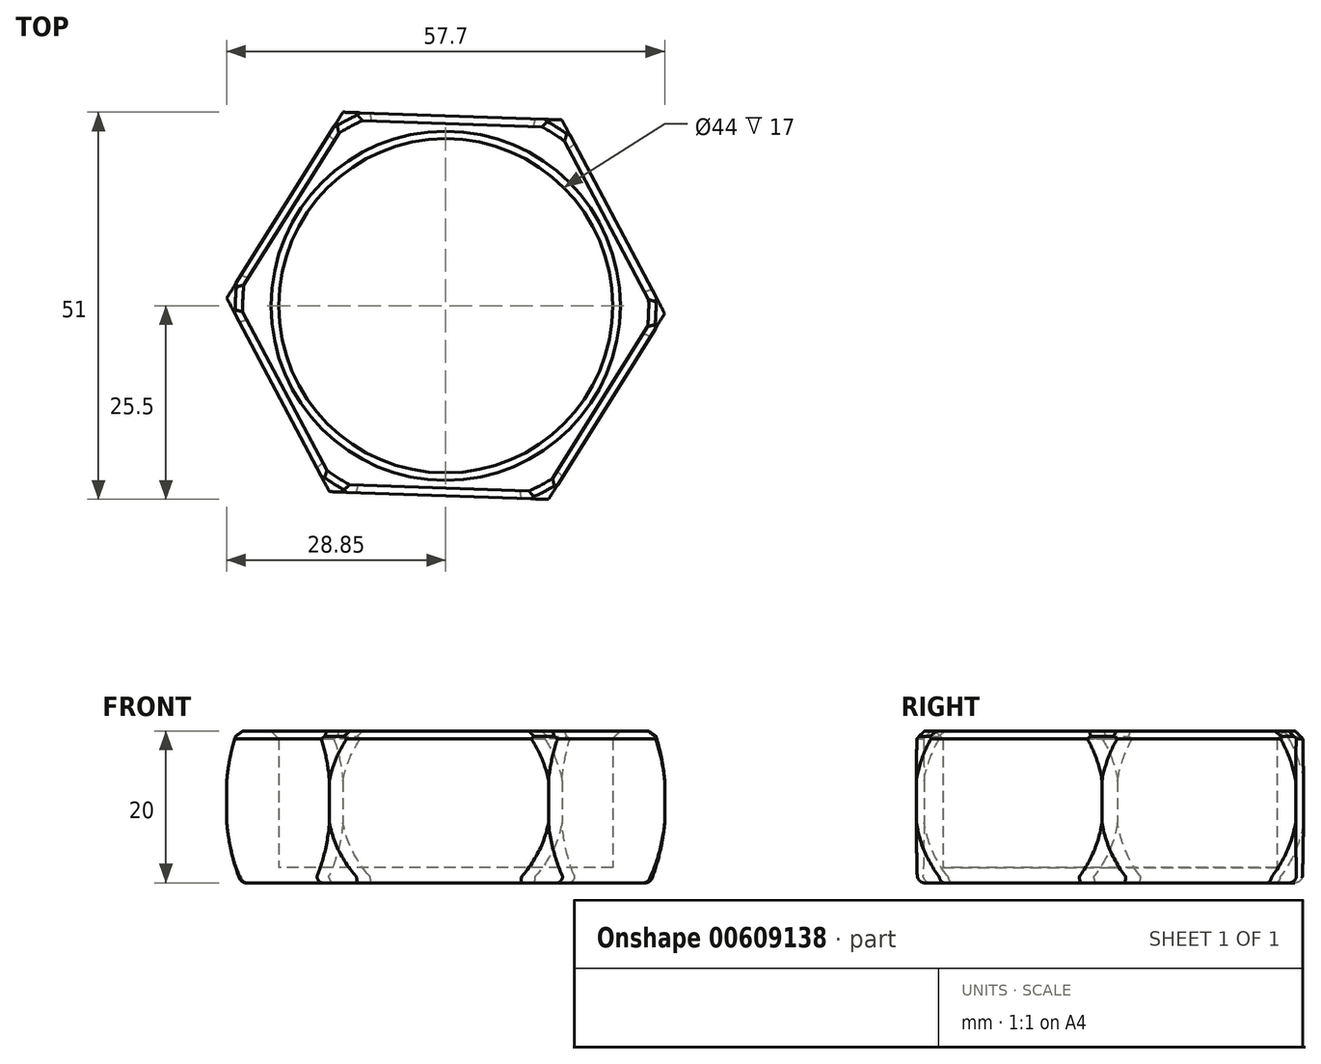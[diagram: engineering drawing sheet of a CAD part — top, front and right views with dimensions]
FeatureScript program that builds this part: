
annotation { "Feature Type Name" : "Feature", "Feature Type Description" : "" }
export const myFeature = defineFeature(function(context is Context, id is Id, definition is map)
    precondition{}
    {
        {
            var Q0;
            Q0=qCreatedBy(makeId("Top.planeOp"),FACE);
            var sketch = newSketch(context, id + "F0", { "sketchPlane" : qUnion([Q0])});
            skCircle(sketch, "E0.cCircle", {"center": v(0, 0) * mm, "radius": 25 * mm, "construction": true});
            skLineSegment(sketch, "E0.0", {"start": v(28.85, -1.03) * mm, "end": v(13.54, -25.5) * mm});
            skLineSegment(sketch, "E0.1", {"start": v(13.54, -25.5) * mm, "end": v(-15.31, -24.47) * mm});
            skLineSegment(sketch, "E0.2", {"start": v(-15.31, -24.47) * mm, "end": v(-28.85, 1.03) * mm});
            skLineSegment(sketch, "E0.3", {"start": v(-28.85, 1.03) * mm, "end": v(-13.54, 25.5) * mm});
            skLineSegment(sketch, "E0.4", {"start": v(-13.54, 25.5) * mm, "end": v(15.31, 24.47) * mm});
            skLineSegment(sketch, "E0.5", {"start": v(15.31, 24.47) * mm, "end": v(28.85, -1.03) * mm});
            skPoint(sketch, "E0.0.midPoint", {"position": v(21.2, -13.26) * mm});
            skSolve(sketch);
        }
        {
            var Q0;
            Q0 = qSketchRegion(id + "F0", true);
            var Q1;
            Q1=makeQuery(id+"F0.imprint","IMPRINT",FACE,{"disambiguationData":[TD([[makeQuery(id+"F0.imprint","IMPRINT",EDGE,{"derivedFrom":sQuery(id+"F0.wireOp",EDGE,"E0.0")}),-1.0]])]});
            extrude(context, id + "F1", {"entities" : qUnion([Q0, Q1]), "depth" : 2 * mm, "offsetDistance" : 25 * mm});
        }
        {
            var Q0;
            Q0=makeQuery(id+"F1.opExtrude","CAP_FACE",FACE,{"disambiguationData":[OSD([sQuery(id+"F0.wireOp",EDGE,"E0.0"),sQuery(id+"F0.wireOp",EDGE,"E0.1"),sQuery(id+"F0.wireOp",EDGE,"E0.2"),sQuery(id+"F0.wireOp",EDGE,"E0.3"),sQuery(id+"F0.wireOp",EDGE,"E0.4"),sQuery(id+"F0.wireOp",EDGE,"E0.5")])],"isStart":false});
            var sketch = newSketch(context, id + "F2", { "sketchPlane" : qUnion([Q0])});
            skLineSegment(sketch, "E1.0", {"start": v(13.54, -25.5) * mm, "end": v(28.85, -1.03) * mm});
            skLineSegment(sketch, "E1.1", {"start": v(15.31, 24.47) * mm, "end": v(-13.54, 25.5) * mm});
            skLineSegment(sketch, "E1.2", {"start": v(-13.54, 25.5) * mm, "end": v(-28.85, 1.03) * mm});
            skLineSegment(sketch, "E1.3", {"start": v(28.85, -1.03) * mm, "end": v(15.31, 24.47) * mm});
            skLineSegment(sketch, "E1.4", {"start": v(-28.85, 1.03) * mm, "end": v(-15.31, -24.47) * mm});
            skLineSegment(sketch, "E1.5", {"start": v(-15.31, -24.47) * mm, "end": v(13.54, -25.5) * mm});
            skCircle(sketch, "E2", {"center": v(0, 0) * mm, "radius": 22 * mm});
            skSolve(sketch);
        }
        {
            var Q0;
            Q0=makeQuery(id+"F2.imprint","IMPRINT",FACE,{"disambiguationData":[TD([[makeQuery(id+"F2.imprint","IMPRINT",EDGE,{"derivedFrom":sQuery(id+"F2.wireOp",EDGE,"E1.0")}),-1.0]])]});
            extrude(context, id + "F3", {"entities" : qUnion([Q0]), "operationType" : NewBodyOperationType.ADD, "depth" : 18 * mm, "offsetDistance" : 25 * mm});
        }
        {
            var Q0;
            Q0=qCreatedBy(makeId("Front.planeOp"),FACE);
            var sketch = newSketch(context, id + "F4", { "sketchPlane" : qUnion([Q0])});
            skArc(sketch, "E3", {"start": v(-4.27, 39.4) * mm, "mid": v(-27.23, 20.67) * mm, "end": v(-21.77, -8.45) * mm});
            skLineSegment(sketch, "E4", {"start": v(-4.27, 39.4) * mm, "end": v(-38.78, 38.35) * mm});
            skLineSegment(sketch, "E5", {"start": v(-38.78, 38.35) * mm, "end": v(-37.35, -8.92) * mm});
            skLineSegment(sketch, "E6", {"start": v(-37.35, -8.92) * mm, "end": v(-21.77, -8.45) * mm});
            skLineSegment(sketch, "E7", {"start": v(0, 10.7) * mm, "end": v(0, -7.35) * mm});
            skSolve(sketch);
        }
        {
            var Q0;
            Q0 = qSketchRegion(id + "F4", true);
            var Q1;
            Q1=sQuery(id+"F4.wireOp",EDGE,"E7");
            revolve(context, id + "F5", {"operationType" : NewBodyOperationType.REMOVE, "entities" : qUnion([Q0]), "axis" : qUnion([Q1]), "revolveType" : RevolveType.FULL, "oppositeDirection" : true});
        }
        {
            var Q0;
            Q0=makeQuery(id+"F1.opExtrude","CAP_FACE",FACE,{"disambiguationData":[OSD([sQuery(id+"F0.wireOp",EDGE,"E0.0"),sQuery(id+"F0.wireOp",EDGE,"E0.1"),sQuery(id+"F0.wireOp",EDGE,"E0.2"),sQuery(id+"F0.wireOp",EDGE,"E0.3"),sQuery(id+"F0.wireOp",EDGE,"E0.4"),sQuery(id+"F0.wireOp",EDGE,"E0.5")])],"isStart":true});
            fillet(context, id + "F6", {"entities" : qUnion([Q0]), "radius" : 1 * mm, "tangentPropagation" : true, "allowEdgeOverflow" : false});
        }
        {
            var Q0;
            Q0=makeQuery(id+"F3.opExtrude","CAP_FACE",FACE,{"disambiguationData":[OSD([sQuery(id+"F2.wireOp",EDGE,"E1.0"),sQuery(id+"F2.wireOp",EDGE,"E1.1"),sQuery(id+"F2.wireOp",EDGE,"E1.2"),sQuery(id+"F2.wireOp",EDGE,"E1.3"),sQuery(id+"F2.wireOp",EDGE,"E1.4"),sQuery(id+"F2.wireOp",EDGE,"E1.5"),sQuery(id+"F2.wireOp",EDGE,"E2")])],"isStart":false});
            chamfer(context, id + "F7", {"entities" : qUnion([Q0]), "width" : 1 * mm, "tangentPropagation" : true});
        }
    });
